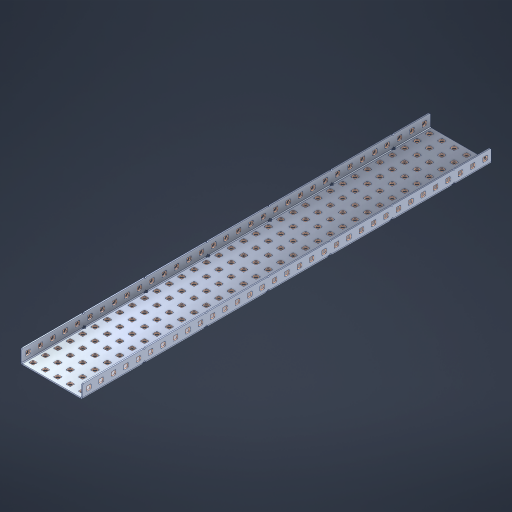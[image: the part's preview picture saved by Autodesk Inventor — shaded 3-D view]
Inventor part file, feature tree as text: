
AUTODESK INVENTOR PART (.ipt)
format: ipt  version: 2023 (Build 270158000, 158)  size: 2,415,616 bytes
history: native  units: in
note: dims shown in document units (in); Inventor stores cm internally (conversion verified against a paired STEP export)
features: other x236, extrude x230, sheet_metal_op x10, sketch x8, mirror x1, pattern_linear x1, chamfer x1
ambient origin geometry x8: Origin, YZ Plane, XZ Plane, XY Plane, X Axis, Y Axis, Z Axis, Center Point
bodies: Solid1 (feature_tree), Body (feature_tree)
feature tree (487):
  other  "Flange Pattern Plane"
  sheet_metal_op  "Flange Pattern"
  sheet_metal_op  "Body Pattern"
  other  "Arc Length"
  mirror  "Notch Mirror"
  pattern_linear  "Notch Pattern"  Spacing1=0.1875in  [1 undecoded]
  chamfer  "End Chamfer"
  extrude  "Half Cut"  Depth=0.0469in
  sketch  "Sketch1"  dims[d0=2.5in]
  other  "Plate1"
  sketch  "Sketch2"  dims[d1=16.5in]
  other  "Plate2"
  sheet_metal_op  "Bend1"
  sheet_metal_op  "Corner1"
  sketch  "Sketch3"  dims[d2=0.0469in]
  other  "Flange Pattern Sketch"
  sketch  "Sketch7"  dims[d3=0.0469in]
  other  "Srf1"
  other  "Srf2"
  sketch  "Sketch8"  dims[d4=0.0234in]
  sketch  "Sketch9"  dims[d5=0.0938in]
  other  "Srf91"
  sheet_metal_op  "Body Pattern Sketch"
  other  "Srf92"
  sketch  "Sketch13"  dims[d6=0.0469in]
  sketch  "Sketch14"  dims[d7=0.5in d8=90.0deg d9=0.0312in d10=0.1875in d11=0.0469in d12=0.0469in d16=0.182in d17=0.02in d18=0.0469in d19=0.0in d20=0.25in d21=0.25in d46=0.172in d47=1.0in d48=0.0in d49=0.182in d50=0.02in d51=0.25in d52=0.25in d53=0.0469in d54=0.0in d55=0.172in d56=1.0in d57=0.0in d60=12.9921in d62=0.5in d63=1.9685in d65=0.5in d85=0.1227in d86=0.1659in d88=0.04in d89=0.0469in d90=0.0in d91=0.04in d92=0.0491in d95=2.5in d96=0.04in d97=0.25in d98=45.0deg d101=0.0in d102=2.497in d131=2.5in d132=12.9921in d134=0.5in d139=0.5in]
  other  "Srf856"
  other  "Srf1310"
  other  "Srf1311"
  other  "Srf1312"
  other  "Srf1376"
  other  "Srf1377"
  other  "Srf1728"
  other  "Srf1755"
  other  "Srf1878"
  other  "Srf1879"
  other  "Srf1880"
  other  "Srf1881"
  other  "Srf1882"
  other  "Srf1883"
  other  "Srf1884"
  other  "Srf1885"
  other  "Srf1886"
  other  "Srf1887"
  other  "Srf1888"
  other  "Srf1889"
  other  "Srf1890"
  other  "Srf1891"
  other  "Srf1892"
  other  "Srf1893"
  other  "Srf1894"
  other  "Srf1895"
  other  "Srf1896"
  other  "Srf1897"
  other  "Srf1898"
  other  "Srf1899"
  other  "Srf1900"
  other  "Srf1901"
  other  "Srf1902"
  other  "Srf1903"
  other  "Srf1904"
  other  "Srf1905"
  other  "Srf1906"
  other  "Srf1942"
  other  "Srf1943"
  other  "Srf1944"
  other  "Srf1945"
  other  "Srf1946"
  other  "Srf1947"
  other  "Srf1948"
  other  "Srf1949"
  other  "Srf1950"
  other  "Srf1951"
  other  "Srf1952"
  other  "Srf1953"
  other  "Srf1954"
  other  "Srf1955"
  other  "Srf1956"
  other  "Srf1957"
  other  "Srf1958"
  other  "Srf1959"
  other  "Srf1960"
  other  "Srf1961"
  other  "Srf1962"
  other  "Srf1963"
  other  "Srf1964"
  other  "Srf1965"
  other  "Srf1966"
  other  "Srf1967"
  other  "Srf1968"
  other  "Srf1969"
  other  "Srf1970"
  other  "Srf2111"
  other  "Srf2112"
  other  "Srf2113"
  other  "Srf2114"
  other  "Srf2115"
  other  "Srf2116"
  other  "Srf2117"
  other  "Srf2118"
  other  "Srf2119"
  other  "Srf2120"
  other  "Srf2121"
  other  "Srf2122"
  other  "Srf2123"
  other  "Srf2124"
  other  "Srf2125"
  other  "Srf2126"
  other  "Srf2127"
  other  "Srf2128"
  other  "Srf2129"
  other  "Srf2130"
  other  "Srf2131"
  other  "Srf2132"
  other  "Srf2133"
  other  "Srf2134"
  other  "Srf2135"
  other  "Srf2136"
  other  "Srf2137"
  other  "Srf2138"
  other  "Srf2139"
  other  "Srf2140"
  other  "Srf2141"
  other  "Srf2146"
  other  "Srf2147"
  other  "Srf2148"
  other  "Srf2149"
  other  "Srf2150"
  other  "Srf2151"
  other  "Srf2152"
  other  "Srf2153"
  other  "Srf2154"
  other  "Srf2155"
  other  "Srf2156"
  other  "Srf2157"
  other  "Srf2158"
  other  "Srf2159"
  other  "Srf2160"
  other  "Srf2161"
  other  "Srf2162"
  other  "Srf2163"
  other  "Srf2164"
  other  "Srf2165"
  other  "Srf2166"
  other  "Srf2167"
  other  "Srf2168"
  other  "Srf2169"
  other  "Srf2170"
  other  "Srf2171"
  other  "Srf2172"
  other  "Srf2173"
  other  "Srf2174"
  other  "Srf2175"
  other  "Srf2176"
  other  "Srf2177"
  other  "Srf2178"
  other  "Srf2179"
  other  "Srf2180"
  other  "Srf2181"
  other  "Srf2182"
  other  "Srf2183"
  other  "Srf2184"
  other  "Srf2185"
  other  "Srf2186"
  other  "Srf2187"
  other  "Srf2188"
  other  "Srf2189"
  other  "Srf2190"
  other  "Srf2191"
  other  "Srf2192"
  other  "Srf2193"
  other  "Srf2194"
  other  "Srf2195"
  other  "Srf2196"
  other  "Srf2197"
  other  "Srf2198"
  other  "Srf2199"
  other  "Srf2200"
  other  "Srf2201"
  other  "Srf2202"
  other  "Srf2203"
  other  "Srf2204"
  other  "Srf2205"
  other  "Srf2206"
  other  "Srf2207"
  other  "Srf2208"
  other  "Srf2209"
  other  "Srf2210"
  other  "Srf2211"
  other  "Srf2212"
  other  "Srf2213"
  other  "Srf2214"
  other  "Srf2215"
  other  "Srf2216"
  other  "Srf2217"
  other  "Srf2218"
  other  "Srf2219"
  other  "Srf2220"
  other  "Srf2221"
  other  "Srf2222"
  other  "Srf2223"
  other  "Srf2224"
  other  "Srf2225"
  other  "Srf2226"
  other  "Srf2227"
  other  "Srf2228"
  other  "Srf2229"
  other  "Srf2230"
  other  "Srf2231"
  other  "Srf2232"
  other  "Srf2233"
  other  "Srf2234"
  other  "Srf2235"
  other  "Srf2236"
  other  "Srf2237"
  other  "Srf2238"
  other  "Srf2239"
  other  "Srf2240"
  other  "Srf2241"
  other  "Srf2242"
  other  "Srf2243"
  other  "Srf2244"
  other  "Srf2245"
  other  "Srf2246"
  other  "Srf2247"
  other  "Srf2248"
  other  "Srf2249"
  other  "Srf2250"
  other  "Srf2251"
  other  "Srf2252"
  other  "Srf2253"
  other  "Srf2254"
  other  "Srf2255"
  other  "Srf2256"
  other  "Srf2257"
  other  "Srf2258"
  other  "Srf2259"
  other  "Srf2260"
  other  "Srf2261"
  other  "Srf2262"
  other  "Srf2263"
  other  "Srf2264"
  other  "Srf2265"
  other  "Srf2266"
  other  "Srf2267"
  other  "Srf2268"
  other  "Srf2269"
  other  "Srf2270"
  other  "Srf2271"
  other  "Srf2272"
  other  "Srf2273"
  other  "Srf2274"
  other  "Srf2275"
  sheet_metal_op  "Flange Stamp"
  sheet_metal_op  "Flange Circle"
  sheet_metal_op  "Body Stamp"
  sheet_metal_op  "Body Circle"
  sheet_metal_op  "Notch"
  extrude  "ExtrusionSrf2"  Depth=0.0469in
  extrude  "ExtrusionSrf92"  Depth=2.5in
  extrude  "ExtrusionSrf856"  Depth=0.02in
  extrude  "ExtrusionSrf1310"  Depth=0.0469in
  extrude  "ExtrusionSrf1311"  TaperAngle=0.0deg  [1 undecoded]
  extrude  "ExtrusionSrf1312"  Depth=0.25in
  extrude  "ExtrusionSrf1376"  Depth=0.25in
  extrude  "ExtrusionSrf1377"  Depth=2.5in
  extrude  "ExtrusionSrf1728"  Depth=2.5in TaperAngle=0.0deg
  extrude  "ExtrusionSrf1755"  Depth=2.5in
  extrude  "ExtrusionSrf1878"  Depth=0.02in
  extrude  "ExtrusionSrf1879"  Depth=0.25in
  extrude  "ExtrusionSrf1880"  Depth=0.25in
  extrude  "ExtrusionSrf1881"  Depth=0.0469in
  extrude  "ExtrusionSrf1882"  TaperAngle=0.0deg  [1 undecoded]
  extrude  "ExtrusionSrf1883"  Depth=2.5in
  extrude  "ExtrusionSrf1884"  Depth=2.5in TaperAngle=0.0deg
  extrude  "ExtrusionSrf1885"  Depth=2.5in
  extrude  "ExtrusionSrf1886"  Depth=2.5in
  extrude  "ExtrusionSrf1887"  Depth=2.5in
  extrude  "ExtrusionSrf1888"  Depth=2.5in
  extrude  "ExtrusionSrf1889"  Depth=2.5in
  extrude  "ExtrusionSrf1890"  Depth=0.0469in
  extrude  "ExtrusionSrf1891"  TaperAngle=0.0deg  [1 undecoded]
  extrude  "ExtrusionSrf1892"  Depth=2.5in
  extrude  "ExtrusionSrf1893"  Depth=2.5in
  extrude  "ExtrusionSrf1894"  Depth=2.5in
  extrude  "ExtrusionSrf1895"  Depth=0.25in TaperAngle=45.0deg
  extrude  "ExtrusionSrf1896"  TaperAngle=0.0deg  [1 undecoded]
  extrude  "ExtrusionSrf1897"  Depth=2.5in
  extrude  "ExtrusionSrf1898"  Depth=2.5in
  extrude  "ExtrusionSrf1899"  Depth=2.5in
  extrude  "ExtrusionSrf1900"  Depth=2.5in
  extrude  "ExtrusionSrf1901"  Depth=2.5in
  extrude  "ExtrusionSrf1902"  [1 undecoded]
  extrude  "ExtrusionSrf1903"  [1 undecoded]
  extrude  "ExtrusionSrf1904"  [1 undecoded]
  extrude  "ExtrusionSrf1905"  [1 undecoded]
  extrude  "ExtrusionSrf1906"  [1 undecoded]
  extrude  "ExtrusionSrf1942"  [1 undecoded]
  extrude  "ExtrusionSrf1943"  [1 undecoded]
  extrude  "ExtrusionSrf1944"  [1 undecoded]
  extrude  "ExtrusionSrf1945"  [1 undecoded]
  extrude  "ExtrusionSrf1946"  [1 undecoded]
  extrude  "ExtrusionSrf1947"  [1 undecoded]
  extrude  "ExtrusionSrf1948"  [1 undecoded]
  extrude  "ExtrusionSrf1949"  [1 undecoded]
  extrude  "ExtrusionSrf1950"  [1 undecoded]
  extrude  "ExtrusionSrf1951"  [1 undecoded]
  extrude  "ExtrusionSrf1952"  [1 undecoded]
  extrude  "ExtrusionSrf1953"  [1 undecoded]
  extrude  "ExtrusionSrf1954"  [1 undecoded]
  extrude  "ExtrusionSrf1955"  [1 undecoded]
  extrude  "ExtrusionSrf1956"  [1 undecoded]
  extrude  "ExtrusionSrf1957"  [1 undecoded]
  extrude  "ExtrusionSrf1958"  [1 undecoded]
  extrude  "ExtrusionSrf1959"  [1 undecoded]
  extrude  "ExtrusionSrf1960"  [1 undecoded]
  extrude  "ExtrusionSrf1961"  [1 undecoded]
  extrude  "ExtrusionSrf1962"  [1 undecoded]
  extrude  "ExtrusionSrf1963"  [1 undecoded]
  extrude  "ExtrusionSrf1964"  [1 undecoded]
  extrude  "ExtrusionSrf1965"  [1 undecoded]
  extrude  "ExtrusionSrf1966"  [1 undecoded]
  extrude  "ExtrusionSrf1967"  [1 undecoded]
  extrude  "ExtrusionSrf1968"  [1 undecoded]
  extrude  "ExtrusionSrf1969"  [1 undecoded]
  extrude  "ExtrusionSrf1970"  [1 undecoded]
  extrude  "ExtrusionSrf2111"  [1 undecoded]
  extrude  "ExtrusionSrf2112"  [1 undecoded]
  extrude  "ExtrusionSrf2113"  [1 undecoded]
  extrude  "ExtrusionSrf2114"  [1 undecoded]
  extrude  "ExtrusionSrf2115"  [1 undecoded]
  extrude  "ExtrusionSrf2116"  [1 undecoded]
  extrude  "ExtrusionSrf2117"  [1 undecoded]
  extrude  "ExtrusionSrf2118"  [1 undecoded]
  extrude  "ExtrusionSrf2119"  [1 undecoded]
  extrude  "ExtrusionSrf2120"  [1 undecoded]
  extrude  "ExtrusionSrf2121"  [1 undecoded]
  extrude  "ExtrusionSrf2122"  [1 undecoded]
  extrude  "ExtrusionSrf2123"  [1 undecoded]
  extrude  "ExtrusionSrf2124"  [1 undecoded]
  extrude  "ExtrusionSrf2125"  [1 undecoded]
  extrude  "ExtrusionSrf2126"  [1 undecoded]
  extrude  "ExtrusionSrf2127"  [1 undecoded]
  extrude  "ExtrusionSrf2128"  [1 undecoded]
  extrude  "ExtrusionSrf2129"  [1 undecoded]
  extrude  "ExtrusionSrf2130"  [1 undecoded]
  extrude  "ExtrusionSrf2131"  [1 undecoded]
  extrude  "ExtrusionSrf2132"  [1 undecoded]
  extrude  "ExtrusionSrf2133"  [1 undecoded]
  extrude  "ExtrusionSrf2134"  [1 undecoded]
  extrude  "ExtrusionSrf2135"  [1 undecoded]
  extrude  "ExtrusionSrf2136"  [1 undecoded]
  extrude  "ExtrusionSrf2137"  [1 undecoded]
  extrude  "ExtrusionSrf2138"  [1 undecoded]
  extrude  "ExtrusionSrf2139"  [1 undecoded]
  extrude  "ExtrusionSrf2140"  [1 undecoded]
  extrude  "ExtrusionSrf2141"  [1 undecoded]
  extrude  "ExtrusionSrf2146"  [1 undecoded]
  extrude  "ExtrusionSrf2147"  [1 undecoded]
  extrude  "ExtrusionSrf2148"  [1 undecoded]
  extrude  "ExtrusionSrf2149"  [1 undecoded]
  extrude  "ExtrusionSrf2150"  [1 undecoded]
  extrude  "ExtrusionSrf2151"  [1 undecoded]
  extrude  "ExtrusionSrf2152"  [1 undecoded]
  extrude  "ExtrusionSrf2153"  [1 undecoded]
  extrude  "ExtrusionSrf2154"  [1 undecoded]
  extrude  "ExtrusionSrf2155"  [1 undecoded]
  extrude  "ExtrusionSrf2156"  [1 undecoded]
  extrude  "ExtrusionSrf2157"  [1 undecoded]
  extrude  "ExtrusionSrf2158"  [1 undecoded]
  extrude  "ExtrusionSrf2159"  [1 undecoded]
  extrude  "ExtrusionSrf2160"  [1 undecoded]
  extrude  "ExtrusionSrf2161"  [1 undecoded]
  extrude  "ExtrusionSrf2162"  [1 undecoded]
  extrude  "ExtrusionSrf2163"  [1 undecoded]
  extrude  "ExtrusionSrf2164"  [1 undecoded]
  extrude  "ExtrusionSrf2165"  [1 undecoded]
  extrude  "ExtrusionSrf2166"  [1 undecoded]
  extrude  "ExtrusionSrf2167"  [1 undecoded]
  extrude  "ExtrusionSrf2168"  [1 undecoded]
  extrude  "ExtrusionSrf2169"  [1 undecoded]
  extrude  "ExtrusionSrf2170"  [1 undecoded]
  extrude  "ExtrusionSrf2171"  [1 undecoded]
  extrude  "ExtrusionSrf2172"  [1 undecoded]
  extrude  "ExtrusionSrf2173"  [1 undecoded]
  extrude  "ExtrusionSrf2174"  [1 undecoded]
  extrude  "ExtrusionSrf2175"  [1 undecoded]
  extrude  "ExtrusionSrf2176"  [1 undecoded]
  extrude  "ExtrusionSrf2177"  [1 undecoded]
  extrude  "ExtrusionSrf2178"  [1 undecoded]
  extrude  "ExtrusionSrf2179"  [1 undecoded]
  extrude  "ExtrusionSrf2180"  [1 undecoded]
  extrude  "ExtrusionSrf2181"  [1 undecoded]
  extrude  "ExtrusionSrf2182"  [1 undecoded]
  extrude  "ExtrusionSrf2183"  [1 undecoded]
  extrude  "ExtrusionSrf2184"  [1 undecoded]
  extrude  "ExtrusionSrf2185"  [1 undecoded]
  extrude  "ExtrusionSrf2186"  [1 undecoded]
  extrude  "ExtrusionSrf2187"  [1 undecoded]
  extrude  "ExtrusionSrf2188"  [1 undecoded]
  extrude  "ExtrusionSrf2189"  [1 undecoded]
  extrude  "ExtrusionSrf2190"  [1 undecoded]
  extrude  "ExtrusionSrf2191"  [1 undecoded]
  extrude  "ExtrusionSrf2192"  [1 undecoded]
  extrude  "ExtrusionSrf2193"  [1 undecoded]
  extrude  "ExtrusionSrf2194"  [1 undecoded]
  extrude  "ExtrusionSrf2195"  [1 undecoded]
  extrude  "ExtrusionSrf2196"  [1 undecoded]
  extrude  "ExtrusionSrf2197"  [1 undecoded]
  extrude  "ExtrusionSrf2198"  [1 undecoded]
  extrude  "ExtrusionSrf2199"  [1 undecoded]
  extrude  "ExtrusionSrf2200"  [1 undecoded]
  extrude  "ExtrusionSrf2201"  [1 undecoded]
  extrude  "ExtrusionSrf2202"  [1 undecoded]
  extrude  "ExtrusionSrf2203"  [1 undecoded]
  extrude  "ExtrusionSrf2204"  [1 undecoded]
  extrude  "ExtrusionSrf2205"  [1 undecoded]
  extrude  "ExtrusionSrf2206"  [1 undecoded]
  extrude  "ExtrusionSrf2207"  [1 undecoded]
  extrude  "ExtrusionSrf2208"  [1 undecoded]
  extrude  "ExtrusionSrf2209"  [1 undecoded]
  extrude  "ExtrusionSrf2210"  [1 undecoded]
  extrude  "ExtrusionSrf2211"  [1 undecoded]
  extrude  "ExtrusionSrf2212"  [1 undecoded]
  extrude  "ExtrusionSrf2213"  [1 undecoded]
  extrude  "ExtrusionSrf2214"  [1 undecoded]
  extrude  "ExtrusionSrf2215"  [1 undecoded]
  extrude  "ExtrusionSrf2216"  [1 undecoded]
  extrude  "ExtrusionSrf2217"  [1 undecoded]
  extrude  "ExtrusionSrf2218"  [1 undecoded]
  extrude  "ExtrusionSrf2219"  [1 undecoded]
  extrude  "ExtrusionSrf2220"  [1 undecoded]
  extrude  "ExtrusionSrf2221"  [1 undecoded]
  extrude  "ExtrusionSrf2222"  [1 undecoded]
  extrude  "ExtrusionSrf2223"  [1 undecoded]
  extrude  "ExtrusionSrf2224"  [1 undecoded]
  extrude  "ExtrusionSrf2225"  [1 undecoded]
  extrude  "ExtrusionSrf2226"  [1 undecoded]
  extrude  "ExtrusionSrf2227"  [1 undecoded]
  extrude  "ExtrusionSrf2228"  [1 undecoded]
  extrude  "ExtrusionSrf2229"  [1 undecoded]
  extrude  "ExtrusionSrf2230"  [1 undecoded]
  extrude  "ExtrusionSrf2231"  [1 undecoded]
  extrude  "ExtrusionSrf2232"  [1 undecoded]
  extrude  "ExtrusionSrf2233"  [1 undecoded]
  extrude  "ExtrusionSrf2234"  [1 undecoded]
  extrude  "ExtrusionSrf2235"  [1 undecoded]
  extrude  "ExtrusionSrf2236"  [1 undecoded]
  extrude  "ExtrusionSrf2237"  [1 undecoded]
  extrude  "ExtrusionSrf2238"  [1 undecoded]
  extrude  "ExtrusionSrf2239"  [1 undecoded]
  extrude  "ExtrusionSrf2240"  [1 undecoded]
  extrude  "ExtrusionSrf2241"  [1 undecoded]
  extrude  "ExtrusionSrf2242"  [1 undecoded]
  extrude  "ExtrusionSrf2243"  [1 undecoded]
  extrude  "ExtrusionSrf2244"  [1 undecoded]
  extrude  "ExtrusionSrf2245"  [1 undecoded]
  extrude  "ExtrusionSrf2246"  [1 undecoded]
  extrude  "ExtrusionSrf2247"  [1 undecoded]
  extrude  "ExtrusionSrf2248"  [1 undecoded]
  extrude  "ExtrusionSrf2249"  [1 undecoded]
  extrude  "ExtrusionSrf2250"  [1 undecoded]
  extrude  "ExtrusionSrf2251"  [1 undecoded]
  extrude  "ExtrusionSrf2252"  [1 undecoded]
  extrude  "ExtrusionSrf2253"  [1 undecoded]
  extrude  "ExtrusionSrf2254"  [1 undecoded]
  extrude  "ExtrusionSrf2255"  [1 undecoded]
  extrude  "ExtrusionSrf2256"  [1 undecoded]
  extrude  "ExtrusionSrf2257"  [1 undecoded]
  extrude  "ExtrusionSrf2258"  [1 undecoded]
  extrude  "ExtrusionSrf2259"  [1 undecoded]
  extrude  "ExtrusionSrf2260"  [1 undecoded]
  extrude  "ExtrusionSrf2261"  [1 undecoded]
  extrude  "ExtrusionSrf2262"  [1 undecoded]
  extrude  "ExtrusionSrf2263"  [1 undecoded]
  extrude  "ExtrusionSrf2264"  [1 undecoded]
  extrude  "ExtrusionSrf2265"  [1 undecoded]
  extrude  "ExtrusionSrf2266"  [1 undecoded]
  extrude  "ExtrusionSrf2267"  [1 undecoded]
  extrude  "ExtrusionSrf2268"  [1 undecoded]
  extrude  "ExtrusionSrf2269"  [1 undecoded]
  extrude  "ExtrusionSrf2270"  [1 undecoded]
  extrude  "ExtrusionSrf2271"  [1 undecoded]
  extrude  "ExtrusionSrf2272"  [1 undecoded]
  extrude  "ExtrusionSrf2273"  [1 undecoded]
  extrude  "ExtrusionSrf2274"  [1 undecoded]
  extrude  "ExtrusionSrf2275"  [1 undecoded]
note: 200 required parameter values undecoded (feature->parameter linkage not recoverable at this tier; creation-order binding heuristic only, values carry confidence <= 0.55)
